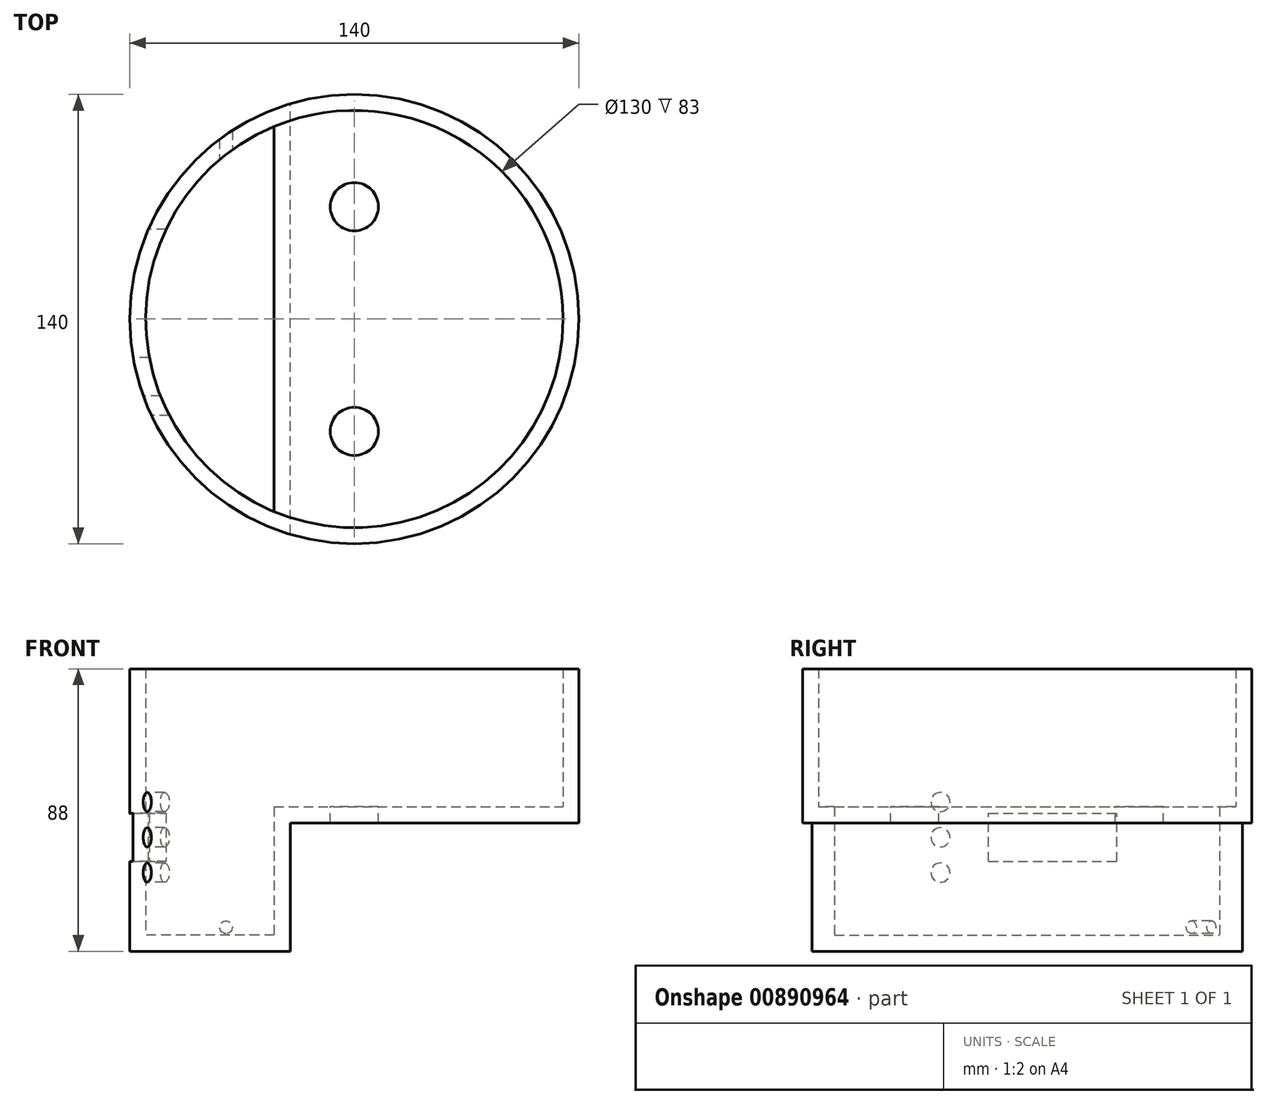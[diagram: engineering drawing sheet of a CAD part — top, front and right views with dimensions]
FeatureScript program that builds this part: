
annotation { "Feature Type Name" : "Feature", "Feature Type Description" : "" }
export const myFeature = defineFeature(function(context is Context, id is Id, definition is map)
    precondition{}
    {
        {
            var Q0;
            Q0=qCreatedBy(makeId("Top.planeOp"),FACE);
            var sketch = newSketch(context, id + "F0", { "sketchPlane" : qUnion([Q0])});
            skCircle(sketch, "E0", {"center": v(0, 0) * mm, "radius": 70 * mm});
            skSolve(sketch);
        }
        {
            var Q0;
            Q0 = qSketchRegion(id + "F0", true);
            extrude(context, id + "F1", {"entities" : qUnion([Q0]), "oppositeDirection" : true, "depth" : 88 * mm, "offsetDistance" : 25 * mm});
        }
        {
            var Q0;
            Q0=qCreatedBy(makeId("Right.planeOp"),FACE);
            cPlane(context, id + "F2", {"entities" : qUnion([Q0]), "cplaneType" : CPlaneType.OFFSET, "offset" : 70 * mm, "width" : 150 * mm, "height" : 150 * mm});
        }
        {
            var Q0;
            Q0=qCreatedBy(id+"F2.planeOp",FACE);
            var sketch = newSketch(context, id + "F3", { "sketchPlane" : qUnion([Q0])});
            skLineSegment(sketch, "E1.bottom", {"start": v(-118.93, -114.95) * mm, "end": v(125.12, -114.95) * mm});
            skLineSegment(sketch, "E1.top", {"start": v(-118.93, -48) * mm, "end": v(125.12, -48) * mm});
            skLineSegment(sketch, "E1.left", {"start": v(-118.93, -114.95) * mm, "end": v(-118.93, -48) * mm});
            skLineSegment(sketch, "E1.right", {"start": v(125.12, -114.95) * mm, "end": v(125.12, -48) * mm});
            skSolve(sketch);
        }
        {
            var Q0;
            Q0 = qSketchRegion(id + "F3", true);
            extrude(context, id + "F4", {"entities" : qUnion([Q0]), "operationType" : NewBodyOperationType.REMOVE, "oppositeDirection" : true, "depth" : 90 * mm, "offsetDistance" : 25 * mm});
        }
        {
            var Q0;
            Q0=makeQuery(id+"F1.opExtrude","CAP_FACE",FACE,{"disambiguationData":[OSD([sQuery(id+"F0.wireOp",EDGE,"E0")])],"isStart":false});
            cPlane(context, id + "F5", {"entities" : qUnion([Q0]), "cplaneType" : CPlaneType.OFFSET, "offset" : 5 * mm, "oppositeDirection" : true, "width" : 150 * mm, "height" : 150 * mm});
        }
        {
            var Q0;
            Q0=qCreatedBy(id+"F5.planeOp",FACE);
            var sketch = newSketch(context, id + "F6", { "sketchPlane" : qUnion([Q0])});
            skArc(sketch, "E2", {"start": v(-25, 60) * mm, "mid": v(-65, 0) * mm, "end": v(-25, -60) * mm});
            skLineSegment(sketch, "E3", {"start": v(-25, 60) * mm, "end": v(-25, -60) * mm});
            skPoint(sketch, "E4.middle", {"position": v(-47, 0) * mm});
            skSolve(sketch);
        }
        {
            var Q0;
            Q0 = qSketchRegion(id + "F6", true);
            extrude(context, id + "F7", {"entities" : qUnion([Q0]), "operationType" : NewBodyOperationType.REMOVE, "endBound" : BoundingType.THROUGH_ALL, "oppositeDirection" : true, "depth" : 25 * mm, "offsetDistance" : 25 * mm});
        }
        {
            var Q0;
            Q0=makeQuery(id+"F1.opExtrude","CAP_FACE",FACE,{"disambiguationData":[OSD([sQuery(id+"F0.wireOp",EDGE,"E0")])],"isStart":true});
            var sketch = newSketch(context, id + "F8", { "sketchPlane" : qUnion([Q0])});
            skCircle(sketch, "E5", {"center": v(0, 0) * mm, "radius": 65 * mm});
            skSolve(sketch);
        }
        {
            var Q0;
            Q0 = qSketchRegion(id + "F8", true);
            extrude(context, id + "F9", {"entities" : qUnion([Q0]), "operationType" : NewBodyOperationType.REMOVE, "oppositeDirection" : true, "depth" : 43 * mm, "offsetDistance" : 25 * mm});
        }
        {
            var Q0;
            Q0=makeQuery(id+"F9.boolean.opBoolean","COPY",FACE,{"derivedFrom":makeQuery(id+"F9.opExtrude","CAP_FACE",FACE,{"disambiguationData":[OSD([sQuery(id+"F8.wireOp",EDGE,"E5")])],"isStart":false})});
            var sketch = newSketch(context, id + "F10", { "sketchPlane" : qUnion([Q0])});
            skCircle(sketch, "E6", {"center": v(0, 35) * mm, "radius": 7.5 * mm});
            skCircle(sketch, "E7.MirrorC", {"center": v(0, -35) * mm, "radius": 7.5 * mm});
            skSolve(sketch);
        }
        {
            var Q0;
            Q0 = qSketchRegion(id + "F10", true);
            extrude(context, id + "F11", {"entities" : qUnion([Q0]), "operationType" : NewBodyOperationType.REMOVE, "endBound" : BoundingType.THROUGH_ALL, "oppositeDirection" : true, "depth" : 25 * mm, "offsetDistance" : 25 * mm});
        }
        {
            var Q0;
            Q0=qCreatedBy(makeId("Right.planeOp"),FACE);
            cPlane(context, id + "F12", {"entities" : qUnion([Q0]), "cplaneType" : CPlaneType.OFFSET, "offset" : 70 * mm, "oppositeDirection" : true, "width" : 150 * mm, "height" : 150 * mm});
        }
        {
            var Q0;
            Q0=qCreatedBy(id+"F12.planeOp",FACE);
            var sketch = newSketch(context, id + "F13", { "sketchPlane" : qUnion([Q0])});
            skLineSegment(sketch, "E8.bottom", {"start": v(28, -45) * mm, "end": v(-12, -45) * mm});
            skLineSegment(sketch, "E8.top", {"start": v(28, -60) * mm, "end": v(-12, -60) * mm});
            skLineSegment(sketch, "E8.left", {"start": v(28, -45) * mm, "end": v(28, -60) * mm});
            skLineSegment(sketch, "E8.right", {"start": v(-12, -45) * mm, "end": v(-12, -60) * mm});
            skCircle(sketch, "E9", {"center": v(-27, -52.5) * mm, "radius": 3 * mm});
            skCircle(sketch, "E10", {"center": v(-27, -41.5) * mm, "radius": 3 * mm});
            skCircle(sketch, "E11", {"center": v(-27, -63.5) * mm, "radius": 3 * mm});
            skSolve(sketch);
        }
        {
            var Q0;
            Q0 = qSketchRegion(id + "F13", true);
            extrude(context, id + "F14", {"entities" : qUnion([Q0]), "operationType" : NewBodyOperationType.REMOVE, "depth" : 25 * mm, "offsetDistance" : 25 * mm});
        }
        {
            var Q0;
            Q0=qCreatedBy(makeId("Front.planeOp"),FACE);
            cPlane(context, id + "F15", {"entities" : qUnion([Q0]), "cplaneType" : CPlaneType.OFFSET, "offset" : 40 * mm, "oppositeDirection" : true, "width" : 150 * mm, "height" : 150 * mm});
        }
        {
            var Q0;
            Q0=qCreatedBy(id+"F15.planeOp",FACE);
            var sketch = newSketch(context, id + "F16", { "sketchPlane" : qUnion([Q0])});
            skCircle(sketch, "E12", {"center": v(-40, -80.5) * mm, "radius": 2 * mm});
            skSolve(sketch);
        }
        {
            var Q0;
            Q0 = qSketchRegion(id + "F16", true);
            extrude(context, id + "F17", {"entities" : qUnion([Q0]), "operationType" : NewBodyOperationType.REMOVE, "oppositeDirection" : true, "depth" : 25 * mm, "offsetDistance" : 25 * mm});
        }
    });
